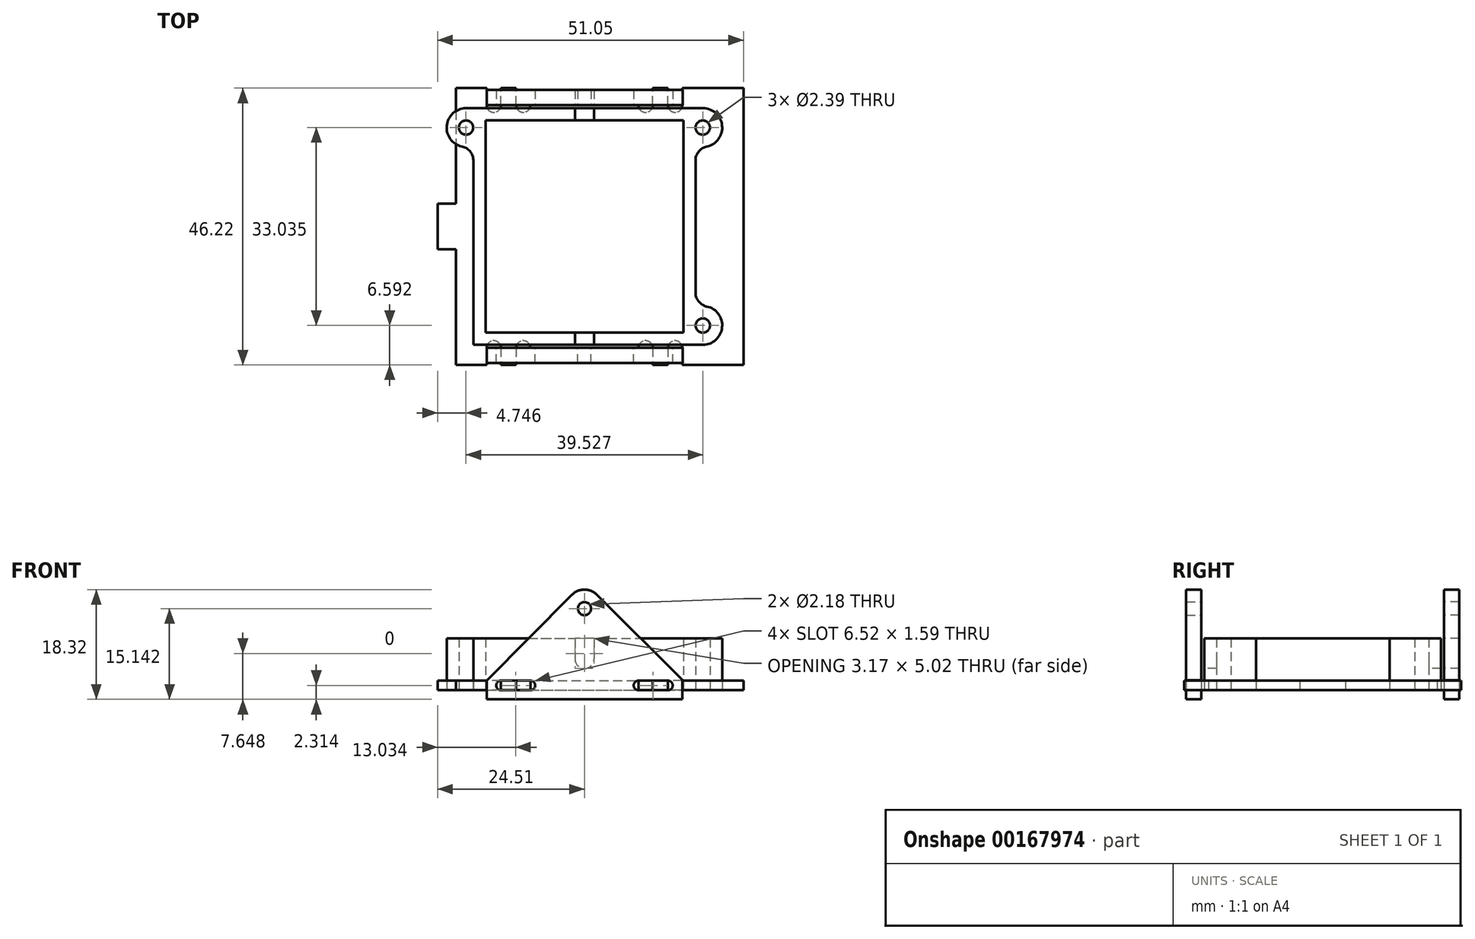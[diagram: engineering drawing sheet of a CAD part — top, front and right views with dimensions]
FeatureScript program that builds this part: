
annotation { "Feature Type Name" : "Feature", "Feature Type Description" : "" }
export const myFeature = defineFeature(function(context is Context, id is Id, definition is map)
    precondition{}
    {
        {
            var Q0;
            Q0=qCreatedBy(makeId("Top.planeOp"),FACE);
            var sketch = newSketch(context, id + "F0", { "sketchPlane" : qUnion([Q0])});
            skLineSegment(sketch, "E0.bottom", {"start": v(-21.45, 23.11) * mm, "end": v(-16.33, 23.11) * mm});
            skLineSegment(sketch, "E0.top", {"start": v(-21.45, -23.11) * mm, "end": v(-16.33, -23.11) * mm});
            skLineSegment(sketch, "E0.left", {"start": v(-21.45, 23.11) * mm, "end": v(-21.45, -23.11) * mm});
            skLineSegment(sketch, "E0.right", {"start": v(21.45, 23.11) * mm, "end": v(21.45, -23.11) * mm, "construction": true});
            skPoint(sketch, "E0.middle", {"position": v(0, 0) * mm});
            skLineSegment(sketch, "E1.bottom", {"start": v(-24.51, 3.8) * mm, "end": v(-21.45, 3.8) * mm});
            skLineSegment(sketch, "E1.top", {"start": v(-24.51, -3.8) * mm, "end": v(-21.45, -3.8) * mm});
            skLineSegment(sketch, "E1.left", {"start": v(-24.51, 3.81) * mm, "end": v(-24.51, -3.8) * mm});
            skPoint(sketch, "E1.middle", {"position": v(-21.45, 0) * mm});
            skLineSegment(sketch, "E2.top", {"start": v(-16.33, 20.26) * mm, "end": v(-15.13, 20.26) * mm, "construction": true});
            skLineSegment(sketch, "E2.left", {"start": v(-16.33, 23.11) * mm, "end": v(-16.33, 20.26) * mm});
            skLineSegment(sketch, "E2.right", {"start": v(16.33, 23.11) * mm, "end": v(16.33, 20.26) * mm});
            skPoint(sketch, "E2.middle", {"position": v(0, 21.69) * mm});
            skLineSegment(sketch, "E3.trimOffspring", {"start": v(16.33, 23.11) * mm, "end": v(21.45, 23.11) * mm});
            skLineSegment(sketch, "E4.MirrorCS", {"start": v(-16.33, -23.11) * mm, "end": v(-16.33, -20.26) * mm});
            skLineSegment(sketch, "E5.MirrorCS", {"start": v(16.33, -23.11) * mm, "end": v(16.33, -20.26) * mm});
            skLineSegment(sketch, "E6.trimOffspring", {"start": v(16.33, -23.11) * mm, "end": v(21.45, -23.11) * mm});
            skArc(sketch, "E7", {"start": v(-16.33, 20.26) * mm, "mid": v(-15.13, 19.06) * mm, "end": v(-13.94, 20.26) * mm});
            skLineSegment(sketch, "E8.trimOffspring", {"start": v(-13.94, 20.26) * mm, "end": v(-11.4, 20.26) * mm, "construction": true});
            skLineSegment(sketch, "E9.bottom", {"start": v(-13.94, 20.26) * mm, "end": v(-11.4, 20.26) * mm});
            skLineSegment(sketch, "E9.top", {"start": v(-13.94, 23.11) * mm, "end": v(-11.4, 23.11) * mm});
            skLineSegment(sketch, "E9.left", {"start": v(-13.94, 20.26) * mm, "end": v(-13.94, 23.11) * mm});
            skLineSegment(sketch, "E9.right", {"start": v(-11.4, 20.26) * mm, "end": v(-11.4, 23.11) * mm});
            skArc(sketch, "E10", {"start": v(-11.4, 20.26) * mm, "mid": v(-10.2, 19.06) * mm, "end": v(-9.01, 20.26) * mm});
            skLineSegment(sketch, "E11.trimOffspring", {"start": v(-9.01, 20.26) * mm, "end": v(9.01, 20.26) * mm});
            skArc(sketch, "E12.MirrorCS", {"start": v(11.4, 20.26) * mm, "mid": v(10.2, 19.06) * mm, "end": v(9.01, 20.26) * mm});
            skLineSegment(sketch, "E13.MirrorCS", {"start": v(11.4, 20.26) * mm, "end": v(11.4, 23.11) * mm});
            skLineSegment(sketch, "E14.MirrorCS", {"start": v(13.94, 20.26) * mm, "end": v(13.94, 23.11) * mm});
            skArc(sketch, "E15.MirrorCS", {"start": v(16.33, 20.26) * mm, "mid": v(15.13, 19.06) * mm, "end": v(13.94, 20.26) * mm});
            skLineSegment(sketch, "E16.MirrorCS", {"start": v(13.94, 23.11) * mm, "end": v(11.4, 23.11) * mm});
            skLineSegment(sketch, "E17.trimOffspring", {"start": v(11.4, 20.26) * mm, "end": v(13.94, 20.26) * mm, "construction": true});
            skLineSegment(sketch, "E18.MirrorCS", {"start": v(-13.94, -20.26) * mm, "end": v(-11.4, -20.26) * mm});
            skLineSegment(sketch, "E19.MirrorCS", {"start": v(-13.94, -20.26) * mm, "end": v(-11.4, -20.26) * mm, "construction": true});
            skArc(sketch, "E20.MirrorCS", {"start": v(16.33, -20.26) * mm, "mid": v(15.13, -19.06) * mm, "end": v(13.94, -20.26) * mm});
            skArc(sketch, "E21.MirrorCS", {"start": v(-16.33, -20.26) * mm, "mid": v(-15.13, -19.06) * mm, "end": v(-13.94, -20.26) * mm});
            skLineSegment(sketch, "E22.MirrorCS", {"start": v(-11.4, -20.26) * mm, "end": v(-11.4, -23.11) * mm});
            skLineSegment(sketch, "E23.MirrorCS", {"start": v(11.4, -20.26) * mm, "end": v(13.94, -20.26) * mm});
            skArc(sketch, "E24.MirrorCS", {"start": v(-11.4, -20.26) * mm, "mid": v(-10.2, -19.06) * mm, "end": v(-9.01, -20.26) * mm});
            skLineSegment(sketch, "E25.MirrorCS", {"start": v(-13.94, -20.26) * mm, "end": v(-13.94, -23.11) * mm});
            skLineSegment(sketch, "E26.MirrorCS", {"start": v(-13.94, -23.11) * mm, "end": v(-11.4, -23.11) * mm});
            skLineSegment(sketch, "E27.MirrorCS", {"start": v(13.94, -20.26) * mm, "end": v(13.94, -23.11) * mm});
            skArc(sketch, "E28.MirrorCS", {"start": v(11.4, -20.26) * mm, "mid": v(10.2, -19.06) * mm, "end": v(9.01, -20.26) * mm});
            skLineSegment(sketch, "E29.MirrorCS", {"start": v(11.4, -20.26) * mm, "end": v(11.4, -23.11) * mm});
            skLineSegment(sketch, "E30.MirrorCS", {"start": v(13.94, -23.11) * mm, "end": v(11.4, -23.11) * mm});
            skLineSegment(sketch, "E31.MirrorCS", {"start": v(-9.01, -20.26) * mm, "end": v(9.01, -20.26) * mm});
            skPoint(sketch, "E32.MirrorP", {"position": v(0, -21.69) * mm});
            skPoint(sketch, "E33.MirrorCS.start.orphan", {"position": v(-16.33, -20.26) * mm});
            skLineSegment(sketch, "E34.trimOffspring", {"start": v(11.4, -20.26) * mm, "end": v(13.94, -20.26) * mm, "construction": true});
            skLineSegment(sketch, "E35.trimOffspring", {"start": v(15.13, -20.26) * mm, "end": v(16.33, -20.26) * mm, "construction": true});
            skLineSegment(sketch, "E36.bottom", {"start": v(16.33, 23.11) * mm, "end": v(26.54, 23.11) * mm});
            skLineSegment(sketch, "E36.top", {"start": v(16.33, -23.11) * mm, "end": v(26.54, -23.11) * mm});
            skLineSegment(sketch, "E36.left", {"start": v(16.33, 23.11) * mm, "end": v(16.33, -23.11) * mm, "construction": true});
            skLineSegment(sketch, "E36.right", {"start": v(26.54, 23.11) * mm, "end": v(26.54, -23.11) * mm});
            skSolve(sketch);
        }
        {
            var Q0;
            Q0=qSketchRegion(id+"F0",true);
            extrude(context, id + "F1", {"entities" : qUnion([Q0]), "offsetDistance" : 25.4 * mm, "depth" : 1.59 * mm});
        }
        {
            var Q0;
            Q0=makeQuery(id+"F1.opExtrude","SWEPT_FACE",FACE,{"disambiguationData":[OSD([sQuery(id+"F0.wireOp",EDGE,"E31.MirrorCS")])]});
            var sketch = newSketch(context, id + "F2", { "sketchPlane" : qUnion([Q0])});
            skLineSegment(sketch, "E37.0", {"start": v(-9.01, 1.59) * mm, "end": v(-11.4, 1.59) * mm});
            skLineSegment(sketch, "E37.1", {"start": v(-13.94, 1.59) * mm, "end": v(-11.4, 1.59) * mm});
            skLineSegment(sketch, "E37.4", {"start": v(-13.94, 1.59) * mm, "end": v(-13.94, 0) * mm});
            skLineSegment(sketch, "E37.5", {"start": v(-9.01, 1.59) * mm, "end": v(-9.01, 0) * mm});
            skLineSegment(sketch, "E37.7", {"start": v(-16.33, 1.59) * mm, "end": v(-16.33, 0) * mm});
            skLineSegment(sketch, "E37.12.1", {"start": v(-13.94, 0) * mm, "end": v(-13.94, 1.59) * mm});
            skLineSegment(sketch, "E37.12.3", {"start": v(-16.33, 1.59) * mm, "end": v(-16.33, 0) * mm});
            skLineSegment(sketch, "E37.13.1", {"start": v(-16.33, 0) * mm, "end": v(-16.33, 1.59) * mm});
            skLineSegment(sketch, "E37.14.0", {"start": v(-13.94, 0) * mm, "end": v(-11.4, 0) * mm});
            skLineSegment(sketch, "E37.14.2", {"start": v(-11.4, 1.59) * mm, "end": v(-13.94, 1.59) * mm});
            skLineSegment(sketch, "E37.14.3", {"start": v(-13.94, 1.59) * mm, "end": v(-13.94, 0) * mm});
            skLineSegment(sketch, "E37.15.0", {"start": v(-9.01, 0) * mm, "end": v(-11.4, 0) * mm});
            skLineSegment(sketch, "E37.15.1", {"start": v(-9.01, 0) * mm, "end": v(-9.01, 1.59) * mm});
            skLineSegment(sketch, "E37.15.2", {"start": v(-11.4, 1.59) * mm, "end": v(-9.01, 1.59) * mm});
            skLineSegment(sketch, "E38.1", {"start": v(13.94, 1.59) * mm, "end": v(13.94, 0) * mm});
            skLineSegment(sketch, "E38.4", {"start": v(16.37, 1.63) * mm, "end": v(24.17, 1.51) * mm, "construction": true});
            skLineSegment(sketch, "E38.6", {"start": v(13.94, 1.59) * mm, "end": v(11.4, 1.59) * mm});
            skLineSegment(sketch, "E38.7", {"start": v(9.01, 1.59) * mm, "end": v(11.4, 1.59) * mm});
            skLineSegment(sketch, "E39.0", {"start": v(9.01, 0) * mm, "end": v(11.4, 0) * mm});
            skLineSegment(sketch, "E39.1", {"start": v(13.94, 0) * mm, "end": v(16.33, 0) * mm});
            skLineSegment(sketch, "E40.bottom", {"start": v(-16.33, 0) * mm, "end": v(16.35, 0) * mm});
            skLineSegment(sketch, "E40.top", {"start": v(-16.33, -1.52) * mm, "end": v(16.35, -1.52) * mm});
            skLineSegment(sketch, "E40.left", {"start": v(-16.33, 0) * mm, "end": v(-16.33, -1.52) * mm});
            skLineSegment(sketch, "E40.right", {"start": v(16.35, 0) * mm, "end": v(16.35, -1.52) * mm});
            skPoint(sketch, "E41", {"position": v(-13.94, 0.8) * mm});
            skPoint(sketch, "E42", {"position": v(0, -1.52) * mm});
            skLineSegment(sketch, "E43", {"start": v(-16.33, 1.59) * mm, "end": v(-2.07, 15.94) * mm});
            skLineSegment(sketch, "E44", {"start": v(2.07, 15.94) * mm, "end": v(16.37, 1.63) * mm});
            skArc(sketch, "E45", {"start": v(2.07, 15.94) * mm, "mid": v(0, 16.8) * mm, "end": v(-2.07, 15.94) * mm});
            skPoint(sketch, "E46.orphan", {"position": v(0, 18.01) * mm});
            skLineSegment(sketch, "E47", {"start": v(9.01, 1.59) * mm, "end": v(9.01, 0) * mm});
            skArc(sketch, "E48", {"start": v(-13.94, 1.59) * mm, "mid": v(-14.73, 0.8) * mm, "end": v(-13.94, 0) * mm});
            skArc(sketch, "E49", {"start": v(-9.01, 0) * mm, "mid": v(-8.22, 0.8) * mm, "end": v(-9.01, 1.59) * mm});
            skArc(sketch, "E50", {"start": v(9.01, 1.59) * mm, "mid": v(8.22, 0.8) * mm, "end": v(9.01, 0) * mm});
            skArc(sketch, "E51", {"start": v(13.94, 0) * mm, "mid": v(14.73, 0.8) * mm, "end": v(13.94, 1.59) * mm});
            skLineSegment(sketch, "E52", {"start": v(16.37, 1.63) * mm, "end": v(16.35, 0) * mm});
            skPoint(sketch, "E53", {"position": v(0, 16.8) * mm});
            skPoint(sketch, "E54", {"position": v(0, 13.62) * mm});
            skCircle(sketch, "E55", {"center": v(0, 13.62) * mm, "radius": 1.1 * mm});
            skSolve(sketch);
        }
        {
            var Q0;
            Q0=qSketchRegion(id+"F2",true);
            extrude(context, id + "F3", {"entities" : qUnion([Q0]), "offsetDistance" : 25.4 * mm, "depth" : 2.54 * mm});
        }
        {
            var Q0;
            Q0=makeQuery(id+"F3.opExtrude","SWEPT_BODY",BODY,{"disambiguationData":[OSD([sQuery(id+"F2.wireOp",EDGE,"E37.13.1"),sQuery(id+"F2.wireOp",EDGE,"E37.14.2"),sQuery(id+"F2.wireOp",EDGE,"E37.15.2"),sQuery(id+"F2.wireOp",EDGE,"E38.6"),sQuery(id+"F2.wireOp",EDGE,"E38.7"),sQuery(id+"F2.wireOp",EDGE,"E40.bottom"),sQuery(id+"F2.wireOp",EDGE,"E40.top"),sQuery(id+"F2.wireOp",EDGE,"E40.left"),sQuery(id+"F2.wireOp",EDGE,"E40.right"),sQuery(id+"F2.wireOp",EDGE,"E43"),sQuery(id+"F2.wireOp",EDGE,"E44"),sQuery(id+"F2.wireOp",EDGE,"E45"),sQuery(id+"F2.wireOp",EDGE,"E48"),sQuery(id+"F2.wireOp",EDGE,"E49"),sQuery(id+"F2.wireOp",EDGE,"E50"),sQuery(id+"F2.wireOp",EDGE,"E51"),sQuery(id+"F2.wireOp",EDGE,"E52")])]});
            var Q1;
            Q1=qCreatedBy(makeId("Front.planeOp"),FACE);
            mirror(context, id + "F4", {"entities" : qUnion([Q0]), "mirrorPlane" : qUnion([Q1])});
        }
        {
            var Q0;
            Q0=qCreatedBy(makeId("Top.planeOp"),FACE);
            var sketch = newSketch(context, id + "F5", { "sketchPlane" : qUnion([Q0])});
            skLineSegment(sketch, "E56.bottom", {"start": v(-16.51, 17.72) * mm, "end": v(16.51, 17.72) * mm});
            skLineSegment(sketch, "E56.top", {"start": v(-16.51, -17.72) * mm, "end": v(16.51, -17.72) * mm});
            skLineSegment(sketch, "E56.left", {"start": v(-16.51, 17.72) * mm, "end": v(-16.51, -17.72) * mm});
            skLineSegment(sketch, "E56.right", {"start": v(16.51, 17.72) * mm, "end": v(16.51, -17.72) * mm});
            skPoint(sketch, "E56.middle", {"position": v(0, 0) * mm});
            skLineSegment(sketch, "E57.bottom", {"start": v(-18.54, 19.75) * mm, "end": v(18.54, 19.75) * mm});
            skLineSegment(sketch, "E57.top", {"start": v(-18.54, -19.75) * mm, "end": v(18.54, -19.75) * mm});
            skLineSegment(sketch, "E57.left", {"start": v(-18.54, 19.75) * mm, "end": v(-18.54, -19.75) * mm});
            skLineSegment(sketch, "E57.right", {"start": v(18.54, 19.75) * mm, "end": v(18.54, -19.75) * mm});
            skLineSegment(sketch, "E58.bottom", {"start": v(-16.51, 17.72) * mm, "end": v(-19.76, 17.72) * mm, "construction": true});
            skLineSegment(sketch, "E58.top", {"start": v(-16.51, 16.52) * mm, "end": v(-19.76, 16.52) * mm, "construction": true});
            skLineSegment(sketch, "E58.left", {"start": v(-16.51, 17.72) * mm, "end": v(-16.51, 16.52) * mm, "construction": true});
            skLineSegment(sketch, "E58.right", {"start": v(-19.76, 17.72) * mm, "end": v(-19.76, 16.52) * mm, "construction": true});
            skCircle(sketch, "E59", {"center": v(-19.76, 16.52) * mm, "radius": 1.2 * mm});
            skLineSegment(sketch, "E60", {"start": v(-19.78, 19.74) * mm, "end": v(-18.54, 19.75) * mm});
            skArc(sketch, "E61", {"start": v(-18.54, 11.14) * mm, "mid": v(-19.1, 12.57) * mm, "end": v(-20.43, 13.36) * mm});
            skArc(sketch, "E62", {"start": v(-19.78, 19.74) * mm, "mid": v(-22.97, 16.85) * mm, "end": v(-20.43, 13.36) * mm});
            skArc(sketch, "E63", {"start": v(-20.43, 13.36) * mm, "mid": v(-16.55, 16.19) * mm, "end": v(-19.78, 19.74) * mm, "construction": true});
            skLineSegment(sketch, "E64.MirrorCS", {"start": v(19.78, 19.74) * mm, "end": v(18.54, 19.75) * mm});
            skArc(sketch, "E65.MirrorCS", {"start": v(18.54, 11.14) * mm, "mid": v(19.1, 12.57) * mm, "end": v(20.43, 13.36) * mm});
            skArc(sketch, "E66.MirrorCS", {"start": v(19.78, 19.74) * mm, "mid": v(22.97, 16.85) * mm, "end": v(20.43, 13.36) * mm});
            skCircle(sketch, "E67.MirrorC", {"center": v(19.76, 16.52) * mm, "radius": 1.2 * mm});
            skArc(sketch, "E68.MirrorCS", {"start": v(-18.54, -11.14) * mm, "mid": v(-19.1, -12.57) * mm, "end": v(-20.43, -13.36) * mm});
            skArc(sketch, "E69.MirrorCS", {"start": v(-19.78, -19.74) * mm, "mid": v(-22.97, -16.85) * mm, "end": v(-20.43, -13.36) * mm});
            skLineSegment(sketch, "E70.MirrorCS", {"start": v(-19.78, -19.74) * mm, "end": v(-18.54, -19.75) * mm});
            skLineSegment(sketch, "E71.MirrorCS", {"start": v(19.78, -19.74) * mm, "end": v(18.54, -19.75) * mm});
            skArc(sketch, "E72.MirrorCS", {"start": v(18.54, -11.14) * mm, "mid": v(19.1, -12.57) * mm, "end": v(20.43, -13.36) * mm});
            skArc(sketch, "E73.MirrorCS", {"start": v(19.78, -19.74) * mm, "mid": v(22.97, -16.85) * mm, "end": v(20.43, -13.36) * mm});
            skCircle(sketch, "E74.MirrorC", {"center": v(19.76, -16.52) * mm, "radius": 1.2 * mm});
            skCircle(sketch, "E75.MirrorC", {"center": v(-19.76, -16.52) * mm, "radius": 1.2 * mm});
            skSolve(sketch);
        }
        {
            var Q0;
            Q0=makeQuery(id+"F5.imprint","IMPRINT",FACE,{"disambiguationData":[TD([[makeQuery(id+"F5.imprint","IMPRINT",EDGE,{"derivedFrom":sQuery(id+"F5.wireOp",EDGE,"E56.bottom")}),1.0]])]});
            var Q1;
            Q1=makeQuery(id+"F5.imprint","IMPRINT",FACE,{"disambiguationData":[TD([[makeQuery(id+"F5.imprint","IMPRINT",EDGE,{"derivedFrom":sQuery(id+"F5.wireOp",EDGE,"E59")}),-1.0]])]});
            var Q2;
            {var subQ1=sQuery(id+"F5.wireOp",EDGE,"E64.MirrorCS");Q2=makeQuery(id+"F5.imprint","IMPRINT",FACE,{"disambiguationData":[TD([[makeQuery(id+"F5.imprint","IMPRINT",EDGE,{"derivedFrom":subQ1}),1.0]])]});}
            var Q3;
            {var subQ1=sQuery(id+"F5.wireOp",EDGE,"E71.MirrorCS");Q3=makeQuery(id+"F5.imprint","IMPRINT",FACE,{"disambiguationData":[TD([[makeQuery(id+"F5.imprint","IMPRINT",EDGE,{"derivedFrom":subQ1}),-1.0]])]});}
            var Q4;
            {var subQ1=sQuery(id+"F5.wireOp",EDGE,"E68.MirrorCS");Q4=makeQuery(id+"F5.imprint","IMPRINT",FACE,{"disambiguationData":[TD([[makeQuery(id+"F5.imprint","IMPRINT",EDGE,{"derivedFrom":subQ1}),1.0]])]});}
            extrude(context, id + "F6", {"entities" : qUnion([Q0, Q1, Q2, Q3, Q4]), "offsetDistance" : 25.4 * mm, "depth" : 8.64 * mm});
        }
        {
            var Q0;
            Q0=makeQuery(id+"F6.opExtrude","SWEPT_FACE",FACE,{"disambiguationData":[OSD([sQuery(id+"F5.wireOp",EDGE,"E57.top")])]});
            var sketch = newSketch(context, id + "F7", { "sketchPlane" : qUnion([Q0])});
            skLineSegment(sketch, "E76.0", {"start": v(-18.54, 8.64) * mm, "end": v(18.54, 8.64) * mm});
            skPoint(sketch, "E77", {"position": v(0, 8.64) * mm});
            skLineSegment(sketch, "E78", {"start": v(0, 8.64) * mm, "end": v(0, 3.62) * mm, "construction": true});
            skCircle(sketch, "E79", {"center": v(0, 5.2) * mm, "radius": 1.59 * mm});
            skLineSegment(sketch, "E80", {"start": v(-1.59, 5.2) * mm, "end": v(-1.59, 8.64) * mm});
            skLineSegment(sketch, "E81", {"start": v(1.59, 5.2) * mm, "end": v(1.59, 8.64) * mm});
            skSolve(sketch);
        }
        {
            var Q0;
            {var subQ0=sQuery(id+"F7.wireOp",EDGE,"E79");var subQ1=makeQuery(id+"F7.imprint","INTERSECT",VERTEX,{"derivedFrom":[subQ0,sQuery(id+"F7.wireOp",EDGE,"E80")]});Q0=makeQuery(id+"F7.imprint","IMPRINT",FACE,{"disambiguationData":[TD([[makeQuery(id+"F7.imprint","IMPRINT",EDGE,{"disambiguationData":[TD([[subQ1,1.0]])],"derivedFrom":subQ0}),1.0]])]});}
            var Q1;
            {var subQ0=sQuery(id+"F7.wireOp",EDGE,"E80");Q1=makeQuery(id+"F7.imprint","IMPRINT",FACE,{"disambiguationData":[TD([[makeQuery(id+"F7.imprint","IMPRINT",EDGE,{"derivedFrom":subQ0}),-1.0]])]});}
            extrude(context, id + "F8", {"entities" : qUnion([Q0, Q1]), "operationType" : NewBodyOperationType.REMOVE, "endBound" : BoundingType.THROUGH_ALL, "oppositeDirection" : true, "offsetDistance" : 25.4 * mm, "depth" : 25.4 * mm});
        }
    });
